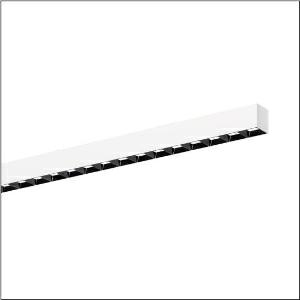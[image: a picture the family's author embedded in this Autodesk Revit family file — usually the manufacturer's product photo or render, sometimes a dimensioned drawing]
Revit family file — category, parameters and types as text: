
# Revit family: silica_r__21_51mx22tbt5w_cdcc
name_source: partatom
category: Lighting Fixtures
units: mm (PartAtom-declared; Revit-internal decimal feet)

## family parameters
Cut with Voids When Loaded = No
Host = Face
Light Source = No
Part Type = Normal
Room Calculation Point = No
Round Connector Dimension = Use Diameter
Shared = No

## types (1)
- --- (1 x LED, 4650 lm, 40.2 W, 6500K)
    Apparent Load = 40 VA
    CIE Flux Codes = 84 100 100 100 100
    Color Rendering = 80
    Color Temperature = 6500K
    Default Elevation = 1800 mm
    Description = Silica® 21, office luminaire, primary light control with darklight reflector, of PMMA, black, CAT 2 (L<= 3000cd/m²), light emission: direct distribution, primary light characteristic: symmetric, installation type: surface-mounted, LED, rated luminous flux: 4.650lm, luminous efficacy: 110lm/W, light colour: 8tw, colour temperature: 2700..6500K, control gear: ECG DALI, with terminal, 3+2-pole, max. 2.5mm², mains connection: 220..240V, AC, 50/60Hz, rated input power: 42.2W, luminaire housing, of aluminium, traffic white (RAL 9016), length: 1.504mm, width: 53mm, height: 53mm, protection rating (complete): IP20, insulation class (complete): insulation class I (protective earthing), certification: CE, permissible operating ambient temperature: 0..+35°C, standard: EN 50419, packaging unit: 1 piece
    Height = 0 mm  [stored 0 ft]
    Lamp = 1 x LED
    Lamp Light Flux = 4650 lm
    Lamp Power = 40.2 W
    Lamp count = 1
    Length = 1504 mm
    Luminous efficacy = 116 lm/W
    Manufacturer = Siteco
    ModVariant = No
    Model = 51MX22TBT5W
    Mounting Place = Ceiling
    Mounting Type = Recessed
    Number of Poles = 1
    OnlyDefault = Yes
    Power Factor = 1
    Product Name = Silica® 21
    Product group = office luminaire | ceiling recessed
    ProductGroupID = 401
    Protection Class = Protection class I
    Protection Degree = IP 20
    RLX_Detail_Level = 1
    RLX_Emergency_Light_Flux = 0 lm
    RLX_Emergency_Type = 0
    RLX_Emergency_Type_DB = No
    RlxData = <blob elided: 41373 chars, md5=2ff633cd>
    Socket = socket
    Standby Power = 0 W
    System Light Flux = 4650 lm
    System Power = 40 W
    Type Comments = individual setting
    Type Image = l_1297779.jpg
    URL = http://relux.com
    VarID = @adj_071479
    Voltage = 0 V
    Weight = 0.00 kg
    Width = 53 mm

note: [stored X ft] marks values corroborated as IEEE doubles in the binary element streams (Revit-internal decimal feet)

## geometry (parser evidence)
native form markers: Blend x4, Sweep x11
no freeform markers — native parametric forms only
